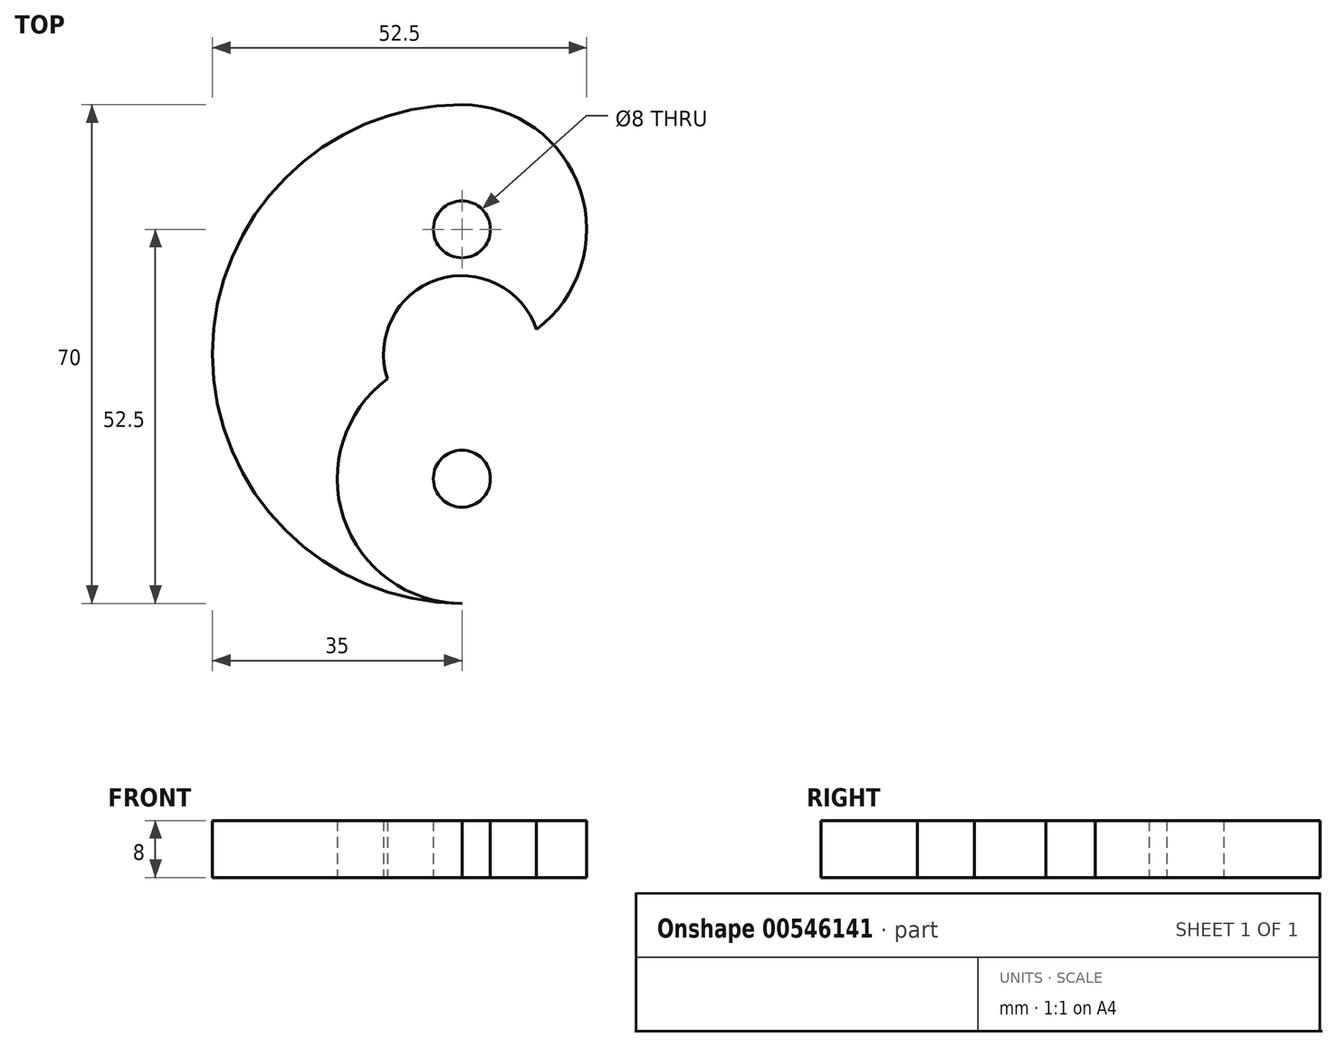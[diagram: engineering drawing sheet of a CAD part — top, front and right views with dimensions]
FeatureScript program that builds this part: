
annotation { "Feature Type Name" : "Feature", "Feature Type Description" : "" }
export const myFeature = defineFeature(function(context is Context, id is Id, definition is map)
    precondition{}
    {
        {
            var Q0;
            Q0=qCreatedBy(makeId("Top.planeOp"),FACE);
            var sketch = newSketch(context, id + "F0", { "sketchPlane" : qUnion([Q0])});
            skCircle(sketch, "E0", {"center": v(0, 0) * mm, "radius": 35 * mm});
            skCircle(sketch, "E1", {"center": v(0, 0) * mm, "radius": 11 * mm});
            skLineSegment(sketch, "E2", {"start": v(-35, 0) * mm, "end": v(35, 0) * mm, "construction": true});
            skLineSegment(sketch, "E3", {"start": v(0, 35) * mm, "end": v(0, -35) * mm, "construction": true});
            skArc(sketch, "E4", {"start": v(10.44, 3.46) * mm, "mid": v(16.61, 23) * mm, "end": v(0, 35) * mm});
            skPoint(sketch, "E4.third.point", {"position": v(-17.44, 18.96) * mm});
            skArc(sketch, "E5.MirrorC", {"start": v(0, -35) * mm, "mid": v(-16.61, -23) * mm, "end": v(-10.44, -3.46) * mm});
            skCircle(sketch, "E6", {"center": v(0, -17.5) * mm, "radius": 4 * mm});
            skCircle(sketch, "E7.MirrorC", {"center": v(0, 17.5) * mm, "radius": 4 * mm});
            skSolve(sketch);
        }
        {
            var Q0;
            {var subQ0=sQuery(id+"F0.wireOp",EDGE,"E4");Q0=makeQuery(id+"F0.imprint","IMPRINT",FACE,{"disambiguationData":[TD([[makeQuery(id+"F0.imprint","IMPRINT",EDGE,{"derivedFrom":subQ0}),1.0]])]});}
            var Q1;
            Q1=makeQuery(id+"F0.imprint","IMPRINT",FACE,{"disambiguationData":[TD([[makeQuery(id+"F0.imprint","IMPRINT",EDGE,{"derivedFrom":sQuery(id+"F0.wireOp",EDGE,"E6")}),1.0]])]});
            extrude(context, id + "F1", {"entities" : qUnion([Q0, Q1]), "depth" : 8 * mm, "offsetDistance" : 25 * mm});
        }
    });
